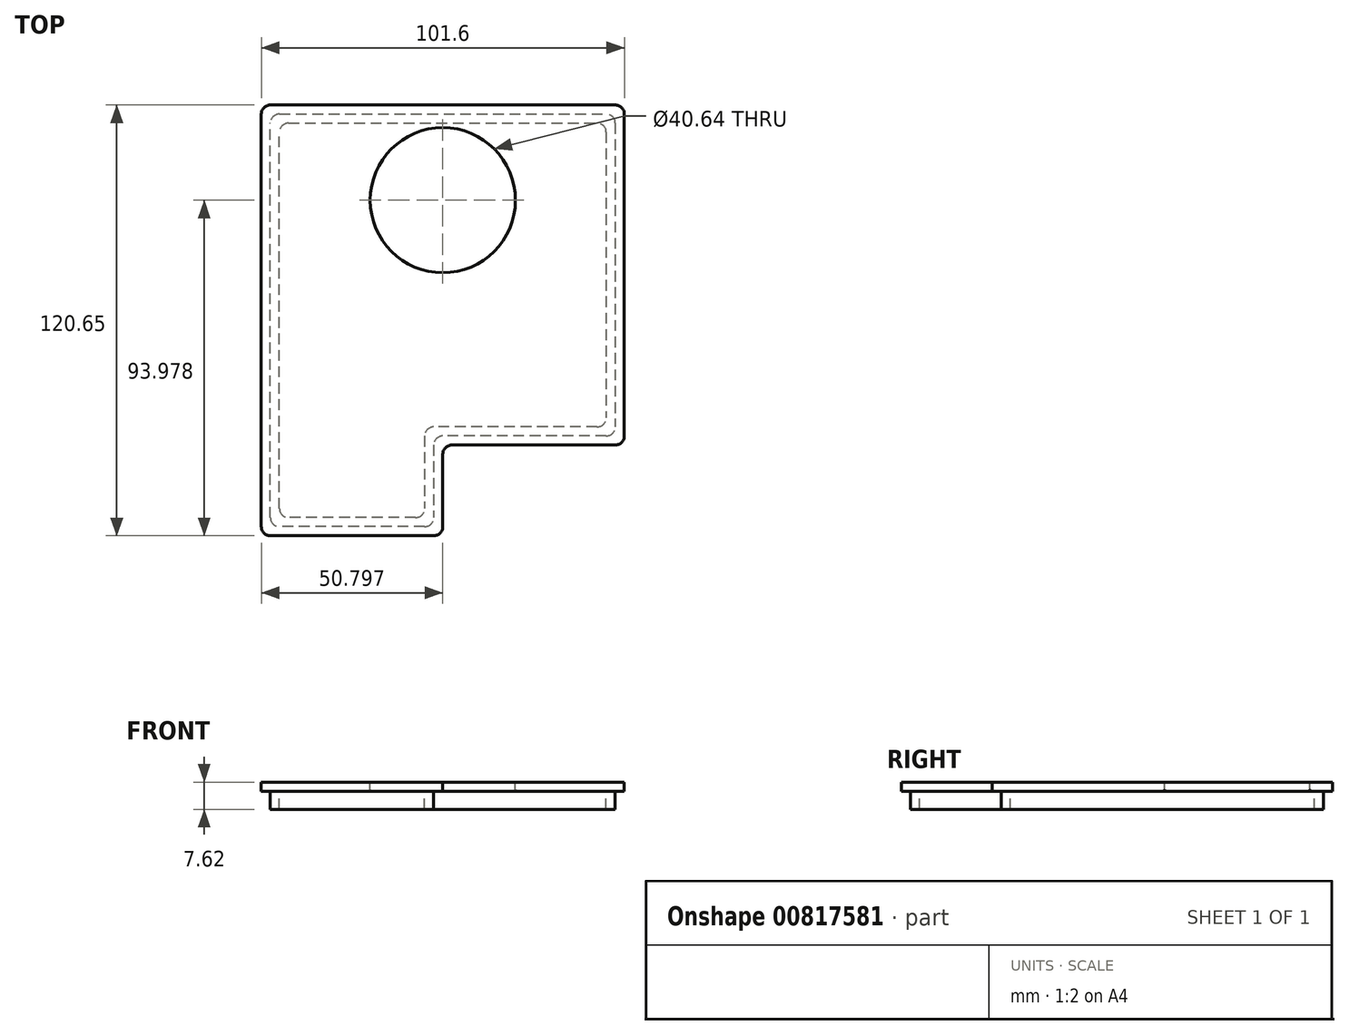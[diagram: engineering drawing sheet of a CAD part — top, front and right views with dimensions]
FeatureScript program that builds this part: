
annotation { "Feature Type Name" : "Feature", "Feature Type Description" : "" }
export const myFeature = defineFeature(function(context is Context, id is Id, definition is map)
    precondition{}
    {
        {
            var Q0;
            Q0=qCreatedBy(makeId("Top.planeOp"),FACE);
            var sketch = newSketch(context, id + "F0", { "sketchPlane" : qUnion([Q0])});
            skLineSegment(sketch, "E0.bottom", {"start": v(-12.72, 93.3) * mm, "end": v(88.88, 93.3) * mm});
            skLineSegment(sketch, "E0.top", {"start": v(-12.72, -27.35) * mm, "end": v(38.08, -27.35) * mm});
            skLineSegment(sketch, "E0.left", {"start": v(-12.72, 93.3) * mm, "end": v(-12.72, -27.35) * mm});
            skLineSegment(sketch, "E0.right", {"start": v(88.88, 93.3) * mm, "end": v(88.88, -1.95) * mm});
            skPoint(sketch, "E0.middle", {"position": v(38.08, 32.97) * mm});
            skLineSegment(sketch, "E1.bottom", {"start": v(88.88, -1.95) * mm, "end": v(38.08, -1.95) * mm});
            skLineSegment(sketch, "E1.right", {"start": v(38.08, -1.95) * mm, "end": v(38.08, -27.35) * mm});
            skPoint(sketch, "E2.orphan", {"position": v(88.88, -27.35) * mm});
            skSolve(sketch);
        }
        {
            var Q0;
            Q0 = qSketchRegion(id + "F0", true);
            extrude(context, id + "F1", {"entities" : qUnion([Q0]), "depth" : 2.54 * mm, "offsetDistance" : 25.4 * mm});
        }
        {
            var Q0;
            Q0=makeQuery(id+"F1.opExtrude","CAP_FACE",FACE,{"disambiguationData":[OSD([sQuery(id+"F0.wireOp",EDGE,"E0.bottom"),sQuery(id+"F0.wireOp",EDGE,"E0.top"),sQuery(id+"F0.wireOp",EDGE,"E0.left"),sQuery(id+"F0.wireOp",EDGE,"E0.right"),sQuery(id+"F0.wireOp",EDGE,"E1.bottom"),sQuery(id+"F0.wireOp",EDGE,"E1.right")])],"isStart":true});
            var sketch = newSketch(context, id + "F2", { "sketchPlane" : qUnion([Q0])});
            skLineSegment(sketch, "E3.0", {"start": v(35.54, 24.81) * mm, "end": v(-10.18, 24.81) * mm});
            skLineSegment(sketch, "E3.1", {"start": v(-10.18, -90.76) * mm, "end": v(86.34, -90.76) * mm});
            skLineSegment(sketch, "E3.2", {"start": v(86.34, -90.76) * mm, "end": v(86.34, -0.59) * mm});
            skLineSegment(sketch, "E3.3", {"start": v(-10.18, 24.81) * mm, "end": v(-10.18, -90.76) * mm});
            skLineSegment(sketch, "E3.4", {"start": v(86.34, -0.59) * mm, "end": v(35.54, -0.59) * mm});
            skLineSegment(sketch, "E3.5", {"start": v(35.54, -0.59) * mm, "end": v(35.54, 24.81) * mm});
            skLineSegment(sketch, "E4.0", {"start": v(33, 22.27) * mm, "end": v(-7.64, 22.27) * mm});
            skLineSegment(sketch, "E4.1", {"start": v(-7.64, -88.22) * mm, "end": v(83.8, -88.22) * mm});
            skLineSegment(sketch, "E4.2", {"start": v(83.8, -88.22) * mm, "end": v(83.8, -3.13) * mm});
            skLineSegment(sketch, "E4.3", {"start": v(-7.64, 22.27) * mm, "end": v(-7.64, -88.22) * mm});
            skLineSegment(sketch, "E4.4", {"start": v(83.8, -3.13) * mm, "end": v(33, -3.13) * mm});
            skLineSegment(sketch, "E4.5", {"start": v(33, -3.13) * mm, "end": v(33, 22.27) * mm});
            skSolve(sketch);
        }
        {
            var Q0;
            Q0 = qSketchRegion(id + "F2", true);
            extrude(context, id + "F3", {"entities" : qUnion([Q0]), "operationType" : NewBodyOperationType.ADD, "depth" : 5.08 * mm, "offsetDistance" : 25.4 * mm});
        }
        {
            var Q0;
            Q0=makeQuery(id+"F1.opExtrude","CAP_FACE",FACE,{"disambiguationData":[OSD([sQuery(id+"F0.wireOp",EDGE,"E0.bottom"),sQuery(id+"F0.wireOp",EDGE,"E0.top"),sQuery(id+"F0.wireOp",EDGE,"E0.left"),sQuery(id+"F0.wireOp",EDGE,"E0.right"),sQuery(id+"F0.wireOp",EDGE,"E1.bottom"),sQuery(id+"F0.wireOp",EDGE,"E1.right")])],"isStart":false});
            var sketch = newSketch(context, id + "F4", { "sketchPlane" : qUnion([Q0])});
            skCircle(sketch, "E5", {"center": v(38.08, 66.63) * mm, "radius": 20.32 * mm});
            skSolve(sketch);
        }
        {
            var Q0;
            Q0 = qSketchRegion(id + "F4", true);
            extrude(context, id + "F5", {"entities" : qUnion([Q0]), "operationType" : NewBodyOperationType.REMOVE, "endBound" : BoundingType.THROUGH_ALL, "oppositeDirection" : true, "depth" : 25.4 * mm, "offsetDistance" : 25.4 * mm});
        }
        {
            var Q0;
            Q0=makeQuery(id+"F1.opExtrude","SWEPT_EDGE",EDGE,{"disambiguationData":[OSD([sQuery(id+"F0.wireOp",EDGE,"E0.top"),sQuery(id+"F0.wireOp",EDGE,"E1.right")])]});
            var Q1;
            Q1=makeQuery(id+"F3.opExtrude","SWEPT_EDGE",EDGE,{"disambiguationData":[OSD([sQuery(id+"F2.wireOp",EDGE,"E3.0"),sQuery(id+"F2.wireOp",EDGE,"E3.5")])]});
            var Q2;
            Q2=makeQuery(id+"F3.opExtrude","SWEPT_EDGE",EDGE,{"disambiguationData":[OSD([sQuery(id+"F2.wireOp",EDGE,"E3.4"),sQuery(id+"F2.wireOp",EDGE,"E3.5")])]});
            var Q3;
            Q3=makeQuery(id+"F1.opExtrude","SWEPT_EDGE",EDGE,{"disambiguationData":[OSD([sQuery(id+"F0.wireOp",EDGE,"E1.bottom"),sQuery(id+"F0.wireOp",EDGE,"E1.right")])]});
            var Q4;
            Q4=makeQuery(id+"F3.opExtrude","SWEPT_EDGE",EDGE,{"disambiguationData":[OSD([sQuery(id+"F2.wireOp",EDGE,"E3.2"),sQuery(id+"F2.wireOp",EDGE,"E3.4")])]});
            var Q5;
            Q5=makeQuery(id+"F1.opExtrude","SWEPT_EDGE",EDGE,{"disambiguationData":[OSD([sQuery(id+"F0.wireOp",EDGE,"E0.right"),sQuery(id+"F0.wireOp",EDGE,"E1.bottom")])]});
            var Q6;
            Q6=makeQuery(id+"F1.opExtrude","SWEPT_EDGE",EDGE,{"disambiguationData":[OSD([sQuery(id+"F0.wireOp",EDGE,"E0.top"),sQuery(id+"F0.wireOp",EDGE,"E0.left")])]});
            var Q7;
            Q7=makeQuery(id+"F3.opExtrude","SWEPT_EDGE",EDGE,{"disambiguationData":[OSD([sQuery(id+"F2.wireOp",EDGE,"E3.0"),sQuery(id+"F2.wireOp",EDGE,"E3.3")])]});
            var Q8;
            Q8=makeQuery(id+"F1.opExtrude","SWEPT_EDGE",EDGE,{"disambiguationData":[OSD([sQuery(id+"F0.wireOp",EDGE,"E0.bottom"),sQuery(id+"F0.wireOp",EDGE,"E0.right")])]});
            var Q9;
            Q9=makeQuery(id+"F3.opExtrude","SWEPT_EDGE",EDGE,{"disambiguationData":[OSD([sQuery(id+"F2.wireOp",EDGE,"E3.1"),sQuery(id+"F2.wireOp",EDGE,"E3.2")])]});
            var Q10;
            Q10=makeQuery(id+"F1.opExtrude","SWEPT_EDGE",EDGE,{"disambiguationData":[OSD([sQuery(id+"F0.wireOp",EDGE,"E0.bottom"),sQuery(id+"F0.wireOp",EDGE,"E0.left")])]});
            var Q11;
            Q11=makeQuery(id+"F3.opExtrude","SWEPT_EDGE",EDGE,{"disambiguationData":[OSD([sQuery(id+"F2.wireOp",EDGE,"E3.1"),sQuery(id+"F2.wireOp",EDGE,"E3.3")])]});
            var Q12;
            Q12=makeQuery(id+"F3.opExtrude","SWEPT_EDGE",EDGE,{"disambiguationData":[OSD([sQuery(id+"F2.wireOp",EDGE,"E4.4"),sQuery(id+"F2.wireOp",EDGE,"E4.5")])]});
            var Q13;
            Q13=makeQuery(id+"F3.opExtrude","SWEPT_EDGE",EDGE,{"disambiguationData":[OSD([sQuery(id+"F2.wireOp",EDGE,"E4.0"),sQuery(id+"F2.wireOp",EDGE,"E4.5")])]});
            var Q14;
            Q14=makeQuery(id+"F3.opExtrude","SWEPT_EDGE",EDGE,{"disambiguationData":[OSD([sQuery(id+"F2.wireOp",EDGE,"E4.0"),sQuery(id+"F2.wireOp",EDGE,"E4.3")])]});
            var Q15;
            Q15=makeQuery(id+"F3.opExtrude","SWEPT_EDGE",EDGE,{"disambiguationData":[OSD([sQuery(id+"F2.wireOp",EDGE,"E4.1"),sQuery(id+"F2.wireOp",EDGE,"E4.3")])]});
            var Q16;
            Q16=makeQuery(id+"F3.opExtrude","SWEPT_EDGE",EDGE,{"disambiguationData":[OSD([sQuery(id+"F2.wireOp",EDGE,"E4.1"),sQuery(id+"F2.wireOp",EDGE,"E4.2")])]});
            var Q17;
            Q17=makeQuery(id+"F3.opExtrude","SWEPT_EDGE",EDGE,{"disambiguationData":[OSD([sQuery(id+"F2.wireOp",EDGE,"E4.2"),sQuery(id+"F2.wireOp",EDGE,"E4.4")])]});
            fillet(context, id + "F6", {"entities" : qUnion([Q0, Q1, Q2, Q3, Q4, Q5, Q6, Q7, Q8, Q9, Q10, Q11, Q12, Q13, Q14, Q15, Q16, Q17]), "radius" : 2.54 * mm, "tangentPropagation" : true, "allowEdgeOverflow" : false});
        }
        {
            var Q0;
            Q0=makeQuery(id+"F5.boolean.opBoolean","INTERSECT",EDGE,{"derivedFrom":[makeQuery(id+"F3.boolean.opBoolean","SPLIT",FACE,{"disambiguationData":[TD([makeQuery(id+"F3.opExtrude","SWEPT_FACE",FACE,{"disambiguationData":[OSD([sQuery(id+"F2.wireOp",EDGE,"E4.0")])]})])],"derivedFrom":makeQuery(id+"F1.opExtrude","CAP_FACE",FACE,{"disambiguationData":[OSD([sQuery(id+"F0.wireOp",EDGE,"E0.bottom"),sQuery(id+"F0.wireOp",EDGE,"E0.top"),sQuery(id+"F0.wireOp",EDGE,"E0.left"),sQuery(id+"F0.wireOp",EDGE,"E0.right"),sQuery(id+"F0.wireOp",EDGE,"E1.bottom"),sQuery(id+"F0.wireOp",EDGE,"E1.right")])],"isStart":true})}),makeQuery(id+"F5.opExtrude","SWEPT_FACE",FACE,{"disambiguationData":[OSD([sQuery(id+"F4.wireOp",EDGE,"E5")])]})]});
            var Q1;
            Q1=makeQuery(id+"F5.boolean.opBoolean","COPY",EDGE,{"derivedFrom":makeQuery(id+"F5.opExtrude","CAP_EDGE",EDGE,{"disambiguationData":[OSD([sQuery(id+"F4.wireOp",EDGE,"E5")])],"isStart":true})});
            fillet(context, id + "F7", {"entities" : qUnion([Q0, Q1]), "radius" : 0.5 * mm, "tangentPropagation" : true, "allowEdgeOverflow" : false});
        }
    });
